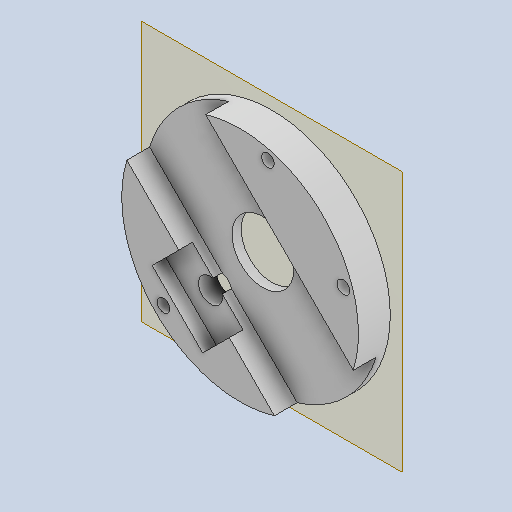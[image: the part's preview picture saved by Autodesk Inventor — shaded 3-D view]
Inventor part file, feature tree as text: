
AUTODESK INVENTOR PART (.ipt)
format: ipt  version: 2022 (Build 260153000, 153)  size: 179,200 bytes
history: native  units: in
note: dims shown in document units (in); Inventor stores cm internally (conversion verified against a paired STEP export)
features: reference x6, other x5, sketch x4, extrude x3, plane x1, hole x1
ambient origin geometry x8: Origin, YZ Plane, XZ Plane, XY Plane, X Axis, Y Axis, Z Axis, Center Point
bodies: Solid1 (feature_tree)
feature tree (20):
  plane  "Work Plane1"
  extrude  "Extrusion1"  TaperAngle=135.0deg  [1 undecoded]
  extrude  "Extrusion2"  Depth=0.1969in TaperAngle=0.0deg
  extrude  "Extrusion3"  Depth=0.1181in TaperAngle=0.0deg
  hole  "Bohrung1"  [1 undecoded]
  sketch  "Sketch1"  dims[d0=0.2756in d1=0.0in d2=135.0deg]
  reference  "Reference1"
  reference  "Reference5"
  reference  "Reference6"
  reference  "Reference7"
  sketch  "Sketch2"  dims[d3=0.9646in d4=0.1969in d5=0.0in]
  sketch  "Sketch3"  dims[d6=0.0039in d7=0.1181in d8=0.0in]
  reference  "Reference8"
  sketch  "Skizze4"  dims[d9=0.1102in d10=0.75in d11=0.375in d12=0.25in d13=0.5635in d14=1.0in d15=0.8108in]
  reference  "Referenz9"
  other  "<userpath>\Documents\Matchboxscope\INVENTOR\Matchboxscope_v1.iam"
  other  "Matchboxscope_v1.iam"
  other  "Matchboxscope_middle2_v1:1"
  other  "Matchboxscope_Lightperiscope_long_V0:1"
  other  "Matchboxscope_middle2_v2:1"
note: 2 required parameter values undecoded (feature->parameter linkage not recoverable at this tier; creation-order binding heuristic only, values carry confidence <= 0.55)
